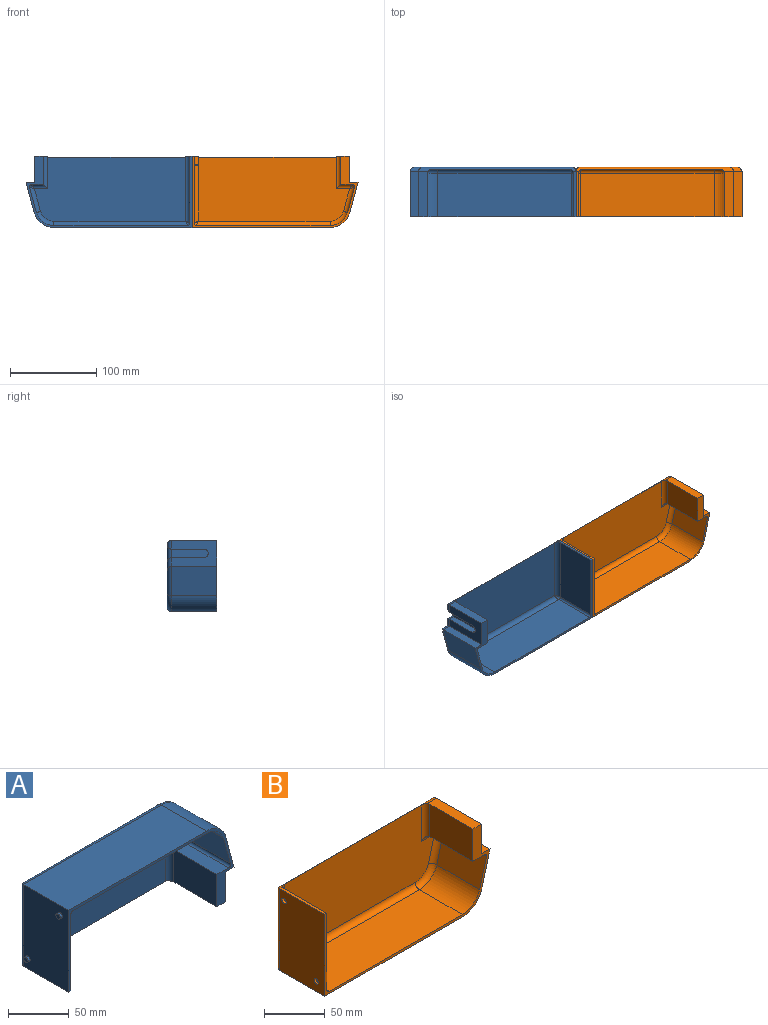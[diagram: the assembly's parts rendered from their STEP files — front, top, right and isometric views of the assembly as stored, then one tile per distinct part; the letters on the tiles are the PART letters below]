
ASSEMBLY  parts=2 mates=1
PART A: 45 faces, bbox 195x57.5x84.5 mm
  f0: plane 52.5x3.17mm, normal (0,0,-1), area 131.8mm2, adj f9,f10,f17,f29,f36
  f1: plane 37.5x7.5mm, normal (0,0,-1), area 281.3mm2, adj f2,f15,f31,f40
  f2: plane 42.5x10mm, normal (1,0,0), area 414.3mm2, adj f1,f3,f33,f40
  f3: plane 37.5x7.5mm, normal (0,0,1), area 281.3mm2, adj f2,f15,f36,f40
  f4: plane 50x32.5mm, normal (-1,0,0), area 1625mm2, adj f5,f16,f17,f24
  f5: plane 50x13.48mm, normal (0,0,1), area 674.2mm2, adj f4,f17,f25,f41
  f6: plane 50x29.5mm, normal (-0.97,0,-0.26), area 1527.2mm2, adj f7,f17,f26,f41
  f7: cylinder r=21.33mm len=50mm, axis (0,1,0), area 1346.2mm2, adj f6,f8,f17,f27
  f8: plane 155.17x50mm, normal (0,0,-1), area 7758.5mm2, adj f7,f17,f28,f43
  f9: plane 77.5x50mm, normal (1,0,0), area 3875mm2, adj f0,f17,f29,f43
  f10: plane 82.5x52.5mm, normal (-1,0,0), area 4292mm2, adj f0,f11,f17,f20,f22,f39
  f11: plane 160.17x52.5mm, normal (0,0,1), area 8408.9mm2, adj f10,f12,f17,f38
  f12: cylinder r=23.83mm len=52.5mm, axis (0,1,0), area 1693.4mm2, adj f11,f13,f17,f37
  f13: plane 52.5x33.81mm, normal (0.97,0,0.26), area 1837.5mm2, adj f12,f14,f17,f34
  f14: plane 52.5x10mm, normal (0,0,-1), area 525mm2, adj f13,f15,f17,f32
  f15: plane 52.5x30mm, normal (1,0,0), area 1160.7mm2, adj f1,f3,f14,f16,f17,f30,f35,f40
  f16: plane 52.5x10.67mm, normal (0,0,-1), area 525.5mm2, adj f4,f15,f17,f24,f36
  f17: plane 192.5x82.5mm, normal (0,-1,0), area 1110.1mm2, adj f0,f4,f5,f6,f7,f8,f9,f10
  f18: plane 175.23x74.33mm, normal (0,-1,0), area 12245.6mm2, adj f24,f25,f26,f27,f28,f29,f36
  f19: plane 180.98x72.5mm, normal (0,1,0), area 12435.2mm2, adj f30,f31,f32,f33,f34,f36,f37,f38
  f20: cylinder r=2.5mm len=5mm, axis (1,0,0), area 39.3mm2, adj f10,f21
  f21: plane 5x5mm, normal (-1,0,0), area 19.6mm2, adj f20
  f22: cylinder r=2.5mm len=5mm, axis (1,0,0), area 39.3mm2, adj f10,f23
  f23: plane 5x5mm, normal (-1,0,0), area 19.6mm2, adj f22
  f24: cylinder r=5mm len=37.5mm, axis (0,0,-1), area 267.7mm2, adj f4,f16,f18,f25,f36
  f25: cylinder r=5mm len=18.48mm, axis (-1,0,0), area 110.9mm2, adj f5,f18,f24,f42
  f26: cylinder r=5mm len=30.8mm, axis (0.26,0,-0.97), area 230.1mm2, adj f6,f18,f27,f42
  f27: torus R=16.33mm, axis (0,1,0), area 193mm2, adj f7,f18,f26,f28
  f28: cylinder r=5mm len=155.17mm, axis (1,0,0), area 1211.6mm2, adj f8,f18,f27,f44
  f29: cylinder r=5mm len=77.5mm, axis (0,0,1), area 599.8mm2, adj f0,f9,f18,f36,f44
  f30: cylinder r=5mm len=15mm, axis (0,0,-1), area 78.5mm2, adj f15,f19,f31,f32
  f31: cylinder r=5mm len=12.5mm, axis (1,0,0), area 58.9mm2, adj f1,f19,f30,f33
  f32: cylinder r=5mm len=15mm, axis (1,0,0), area 74.2mm2, adj f14,f19,f30,f34
  f33: cylinder r=5mm len=20mm, axis (0,0,1), area 107.1mm2, adj f2,f19,f31,f36
  f34: cylinder r=5mm len=35.22mm, axis (-0.26,0,0.97), area 256.8mm2, adj f13,f19,f32,f37
  f35: cylinder r=5mm len=10mm, axis (0,0,1), area 50mm2, adj f15,f36
  f36: cylinder r=5mm len=182.5mm, axis (-1,0,0), area 1029mm2, adj f0,f3,f16,f18,f19,f24,f29,f33
  f37: torus R=18.83mm, axis (0,1,0), area 234.5mm2, adj f12,f19,f34,f38
  f38: cylinder r=5mm len=160.17mm, axis (-1,0,0), area 1243.7mm2, adj f11,f19,f37,f39
  f39: cylinder r=5mm len=82.5mm, axis (0,0,-1), area 619.4mm2, adj f10,f19,f36,f38
  f40: cylinder r=5mm len=10mm, axis (-1,0,0), area 117.8mm2, adj f1,f2,f3,f15
  f41: cylinder r=2.5mm len=50mm, axis (0,-1,0), area 229.1mm2, adj f5,f6,f17,f42
  f42: bspline ~6.52x6.19mm, area 24.8mm2, adj f25,f26,f41
  f43: cylinder r=2.5mm len=50mm, axis (0,-1,0), area 196.3mm2, adj f8,f9,f17,f44
  f44: bspline ~5.97x5mm, area 20.5mm2, adj f28,f29,f43
PART B: 45 faces, bbox 192.5x57.5x84.5 mm
  f0: plane 52.5x10.67mm, normal (0,0,1), area 525.5mm2, adj f4,f15,f17,f24,f33
  f1: plane 37.5x7.5mm, normal (0,0,1), area 281.3mm2, adj f2,f15,f30,f40
  f2: plane 42.5x10mm, normal (1,0,0), area 414.3mm2, adj f1,f3,f31,f40
  f3: plane 37.5x7.5mm, normal (0,0,-1), area 281.3mm2, adj f2,f15,f33,f40
  f4: plane 50x32.5mm, normal (-1,0,0), area 1625mm2, adj f0,f5,f17,f24
  f5: plane 50x13.48mm, normal (0,0,-1), area 674.2mm2, adj f4,f17,f26,f41
  f6: plane 50x29.5mm, normal (-0.97,0,0.26), area 1527.2mm2, adj f7,f17,f28,f41
  f7: cylinder r=21.33mm len=50mm, axis (0,1,0), area 1346.2mm2, adj f6,f8,f17,f29
  f8: plane 155.17x50mm, normal (0,0,1), area 7758.5mm2, adj f7,f17,f27,f43
  f9: plane 77.5x50mm, normal (1,0,0), area 3834.2mm2, adj f16,f17,f20,f21,f22,f25,f43
  f10: plane 82.5x52.5mm, normal (-1,0,0), area 4290.4mm2, adj f11,f16,f17,f20,f21,f37
  f11: plane 160.17x52.5mm, normal (0,0,-1), area 8408.9mm2, adj f10,f12,f17,f39
  f12: cylinder r=23.83mm len=52.5mm, axis (0,1,0), area 1693.4mm2, adj f11,f13,f17,f38
  f13: plane 52.5x33.81mm, normal (0.97,0,-0.26), area 1837.5mm2, adj f12,f14,f17,f36
  f14: plane 52.5x10mm, normal (0,0,1), area 525mm2, adj f13,f15,f17,f35
  f15: plane 52.5x30mm, normal (1,0,0), area 1160.7mm2, adj f0,f1,f3,f14,f17,f32,f34,f40
  f16: plane 52.5x3.17mm, normal (0,0,1), area 131.8mm2, adj f9,f10,f17,f22,f33
  f17: plane 192.5x82.5mm, normal (0,-1,0), area 1110.1mm2, adj f0,f4,f5,f6,f7,f8,f9,f10
  f18: plane 175.23x74.33mm, normal (0,-1,0), area 12245.6mm2, adj f22,f23,f24,f25,f26,f27,f28,f29
  f19: plane 180.98x72.5mm, normal (0,1,0), area 12435.2mm2, adj f30,f31,f32,f33,f35,f36,f37,f38
  f20: cylinder r=2.55mm len=5.1mm, axis (-1,0,0), area 40.1mm2, adj f9,f10
  f21: cylinder r=2.55mm len=5.1mm, axis (-1,0,0), area 40.1mm2, adj f9,f10,f23
  f22: cylinder r=5mm len=9.5mm, axis (0,0,-1), area 72.8mm2, adj f9,f16,f18,f23,f33
  f23: bspline ~5.23x5.22mm, area 7.9mm2, adj f18,f21,f22,f25
  f24: cylinder r=5mm len=37.5mm, axis (0,0,1), area 267.8mm2, adj f0,f4,f18,f26,f33
  f25: cylinder r=5mm len=67mm, axis (0,0,-1), area 519.1mm2, adj f9,f18,f23,f44
  f26: cylinder r=5mm len=18.48mm, axis (-1,0,0), area 110.9mm2, adj f5,f18,f24,f42
  f27: cylinder r=5mm len=155.17mm, axis (1,0,0), area 1211.6mm2, adj f8,f18,f29,f44
  f28: cylinder r=5mm len=30.8mm, axis (0.26,0,0.97), area 230.1mm2, adj f6,f18,f29,f42
  f29: torus R=16.33mm, axis (0,1,0), area 193mm2, adj f7,f18,f27,f28
  f30: cylinder r=5mm len=12.5mm, axis (1,0,0), area 58.9mm2, adj f1,f19,f31,f32
  f31: cylinder r=5mm len=20mm, axis (0,0,-1), area 107.1mm2, adj f2,f19,f30,f33
  f32: cylinder r=5mm len=15mm, axis (0,0,1), area 78.5mm2, adj f15,f19,f30,f35
  f33: cylinder r=5mm len=182.5mm, axis (-1,0,0), area 1029mm2, adj f0,f3,f16,f18,f19,f22,f24,f31
  f34: cylinder r=5mm len=10mm, axis (0,0,-1), area 50mm2, adj f15,f33
  f35: cylinder r=5mm len=15mm, axis (1,0,0), area 74.2mm2, adj f14,f19,f32,f36
  f36: cylinder r=5mm len=35.22mm, axis (-0.26,0,-0.97), area 256.8mm2, adj f13,f19,f35,f38
  f37: cylinder r=5mm len=82.5mm, axis (0,0,1), area 619.4mm2, adj f10,f19,f33,f39
  f38: torus R=18.83mm, axis (0,1,0), area 234.5mm2, adj f12,f19,f36,f39
  f39: cylinder r=5mm len=160.17mm, axis (-1,0,0), area 1243.7mm2, adj f11,f19,f37,f38
  f40: cylinder r=5mm len=10mm, axis (1,0,0), area 117.8mm2, adj f1,f2,f3,f15
  f41: cylinder r=2.5mm len=50mm, axis (0,-1,0), area 229.1mm2, adj f5,f6,f17,f42
  f42: bspline ~6.52x6.19mm, area 24.8mm2, adj f26,f28,f41
  f43: cylinder r=2.5mm len=50mm, axis (0,-1,0), area 196.3mm2, adj f8,f9,f17,f44
  f44: bspline ~5.97x5mm, area 20.6mm2, adj f25,f27,f43
PLACE A rot(axis=(0,1,0),180deg) t=(-81.25,8.25,11.41)mm
PLACE B t=(-81.25,8.25,11.41)mm
MATE fastened A.f20 <-> B.f20  axis (1,0,0) through (-78.75,-36.75,-71.25)mm
